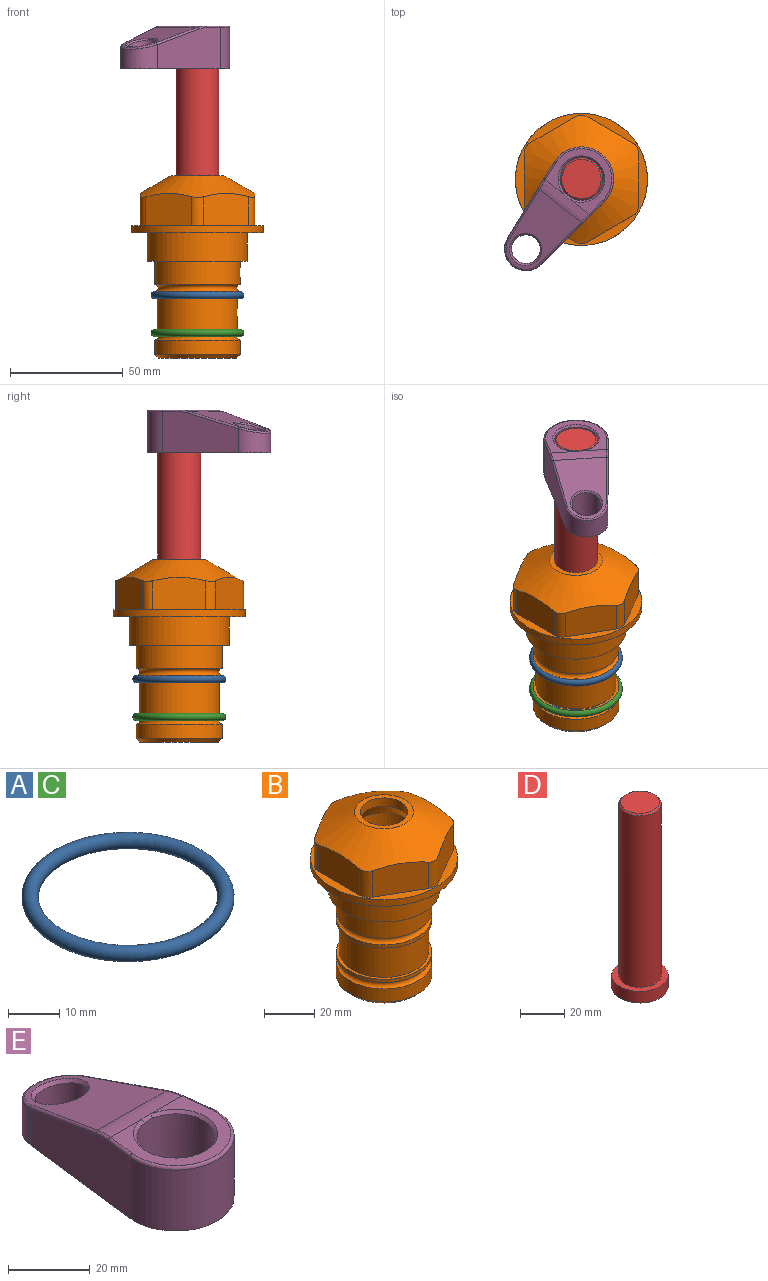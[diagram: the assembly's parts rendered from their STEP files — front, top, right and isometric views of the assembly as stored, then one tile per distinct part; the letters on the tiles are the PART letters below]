
ASSEMBLY  parts=5 mates=4
PART A: 1 faces, bbox 44.7x44.7x3.2 mm
  f0: torus R=19.05mm, axis (0,0,1), area 1193.9mm2
PART B: 36 faces, bbox 58.7x58.7x81 mm
  f0: cylinder r=17.78mm len=35.56mm, axis (0,0,1), area 1670.8mm2, adj f23,f24,f31
  f1: cylinder r=19.05mm len=38.1mm, axis (0,0,1), area 1191.9mm2, adj f26,f27,f30
  f2: plane 58.66x58.66mm, normal (0,0,-1), area 1150.6mm2, adj f3,f28
  f3: cylinder r=29.33mm len=58.66mm, axis (0,0,-1), area 585.1mm2, adj f2,f4
  f4: plane 58.66x58.66mm, normal (0,0,1), area 475.9mm2, adj f3,f5,f6,f7,f8,f9,f10,f11
  f5: plane 20.32x14.34mm, normal (-0.5,0.87,0), area 324.4mm2, adj f4,f15,f16,f17
  f6: plane 20.32x14.34mm, normal (0.5,0.87,0), area 324.4mm2, adj f4,f14,f15,f17
  f7: plane 23.48x14.34mm, normal (1,0,0), area 324.4mm2, adj f4,f13,f14,f17
  f8: plane 20.32x14.34mm, normal (0.5,-0.87,0), area 324.4mm2, adj f4,f12,f13,f17
  f9: plane 20.32x14.34mm, normal (-0.5,-0.87,0), area 324.4mm2, adj f4,f11,f12,f17
  f10: plane 23.48x14.34mm, normal (-1,0,0), area 324.4mm2, adj f4,f11,f16,f17
  f11: cylinder r=5.08mm len=12.85mm, axis (0,0,-1), area 67.2mm2, adj f4,f9,f10,f17
  f12: cylinder r=5.08mm len=12.85mm, axis (0,0,-1), area 67.2mm2, adj f4,f8,f9,f17
  f13: cylinder r=5.08mm len=12.85mm, axis (0,0,-1), area 67.2mm2, adj f4,f7,f8,f17
  f14: cylinder r=5.08mm len=12.85mm, axis (0,0,-1), area 67.2mm2, adj f4,f6,f7,f17
  f15: cylinder r=5.08mm len=12.85mm, axis (0,0,-1), area 67.2mm2, adj f4,f5,f6,f17
  f16: cylinder r=5.08mm len=12.85mm, axis (0,0,-1), area 67.2mm2, adj f4,f5,f10,f17
  f17: cone r=11.73mm half-angle=60deg, axis (0,0,-1), area 2071.8mm2, adj f5,f6,f7,f8,f9,f10,f11,f12
  f18: plane 23.46x23.46mm, normal (0,0,1), area 147.4mm2, adj f17,f35
  f19: plane 34.93x34.93mm, normal (0,0,-1), area 958mm2, adj f29
  f20: cylinder r=19.05mm len=38.1mm, axis (0,0,1), area 760.1mm2, adj f21,f29
  f21: torus R=19.05mm, axis (0,0,1), area 565.3mm2, adj f20,f22
  f22: cylinder r=19.05mm len=38.1mm, axis (0,0,1), area 190mm2, adj f21,f23
  f23: plane 38.1x38.1mm, normal (0,0,1), area 146.9mm2, adj f0,f22
  f24: plane 38.1x38.1mm, normal (0,0,-1), area 146.9mm2, adj f0,f25
  f25: cylinder r=19.05mm len=38.1mm, axis (0,0,1), area 190mm2, adj f24,f26
  f26: torus R=19.05mm, axis (0,0,1), area 565.3mm2, adj f1,f25
  f27: plane 44.45x44.45mm, normal (0,0,-1), area 411.7mm2, adj f1,f28
  f28: cylinder r=22.23mm len=44.45mm, axis (0,0,1), area 1773.5mm2, adj f2,f27
  f29: cone r=19.05mm half-angle=45deg, axis (0,0,1), area 257.5mm2, adj f19,f20
  f30: cylinder r=3.17mm len=6.75mm, axis (-1,0,0), area 128mm2, adj f1,f33
  f31: cylinder r=3.17mm len=6.35mm, axis (-1,0,0), area 102.5mm2, adj f0,f33
  f32: plane 25.4x25.4mm, normal (0,0,1), area 506.7mm2, adj f33
  f33: cylinder r=12.7mm len=66.42mm, axis (0,0,-1), area 5236.2mm2, adj f30,f31,f32,f34
  f34: cone r=9.53mm half-angle=30deg, axis (0,0,-1), area 443.4mm2, adj f33,f35
  f35: cylinder r=9.53mm len=19.05mm, axis (0,0,-1), area 240.9mm2, adj f18,f34
PART C: same geometry as A
PART D: 6 faces, bbox 25.4x25.4x101.6 mm
  f0: plane 17.46x17.46mm, normal (0,0,1), area 239.5mm2, adj f5
  f1: plane 25.4x25.4mm, normal (0,0,-1), area 506.7mm2, adj f2
  f2: cylinder r=12.7mm len=25.4mm, axis (0,0,1), area 506.7mm2, adj f1,f3
  f3: plane 25.4x25.4mm, normal (0,0,1), area 221.7mm2, adj f2,f4
  f4: cylinder r=9.53mm len=94.46mm, axis (0,0,1), area 5653mm2, adj f3,f5
  f5: cone r=8.73mm half-angle=45deg, axis (0,0,-1), area 64.4mm2, adj f0,f4
PART E: 31 faces, bbox 31.7x65.5x19.8 mm
  f0: plane 39.12x18.26mm, normal (0.99,0.12,0), area 612.2mm2, adj f1,f4,f7,f11,f13,f15
  f1: cylinder r=9.53mm len=18.91mm, axis (0,0,-1), area 296.1mm2, adj f0,f2,f7,f17
  f2: plane 39.12x18.26mm, normal (-0.99,0.12,0), area 612.2mm2, adj f1,f4,f7,f12,f14,f16
  f3: cylinder r=6.35mm len=12.7mm, axis (0,0,-1), area 362.4mm2, adj f7,f18
  f4: cylinder r=14.29mm len=28.58mm, axis (0,0,-1), area 882.2mm2, adj f0,f2,f7,f10
  f5: cylinder r=9.53mm len=19.05mm, axis (0,0,-1), area 1092.6mm2, adj f7,f19,f20
  f6: plane 26.99x23.69mm, normal (0,0,1), area 216.2mm2, adj f9,f10,f11,f12,f19
  f7: plane 63.5x28.58mm, normal (0,0,-1), area 661.8mm2, adj f0,f1,f2,f3,f4,f5,f22,f23
  f8: plane 33.52x23.6mm, normal (0,0.26,0.97), area 486mm2, adj f9,f15,f16,f17,f18
  f9: cylinder r=19.05mm len=24.72mm, axis (1,0,0), area 120.4mm2, adj f6,f8,f13,f14,f20
  f10: torus R=13.49mm, axis (0,0,1), area 59mm2, adj f4,f6,f11,f12
  f11: cylinder r=0.79mm len=8.67mm, axis (0.12,-0.99,0), area 10.8mm2, adj f0,f6,f10,f13
  f12: cylinder r=0.79mm len=8.67mm, axis (0.12,0.99,0), area 10.8mm2, adj f2,f6,f10,f14
  f13: bspline ~4.95x1.42mm, area 6.1mm2, adj f0,f9,f11,f15
  f14: bspline ~4.95x1.42mm, area 6.1mm2, adj f2,f9,f12,f16
  f15: cylinder r=0.79mm len=25.95mm, axis (0.12,-0.96,0.26), area 32.9mm2, adj f0,f8,f13,f17
  f16: cylinder r=0.79mm len=25.95mm, axis (0.12,0.96,-0.26), area 32.9mm2, adj f2,f8,f14,f17
  f17: bspline ~18.91x8.38mm, area 30mm2, adj f1,f8,f15,f16
  f18: bspline ~14.29x14.29mm, area 48.3mm2, adj f3,f8
  f19: cone r=9.53mm half-angle=45deg, axis (0,0,1), area 66.5mm2, adj f5,f6,f20
  f20: bspline ~3.22x0.96mm, area 3.5mm2, adj f5,f9,f19
  f21: plane 2.75x2.72mm, normal (0,0,-1), area 2.9mm2, adj f23,f25,f28
  f22: plane 23.05x15.88mm, normal (-0.99,-0.12,0), area 323.6mm2, adj f7,f25,f26,f27,f28,f29
  f23: plane 23.05x15.88mm, normal (0.99,-0.12,0), area 323.6mm2, adj f7,f21,f25,f27,f28,f30
  f24: cylinder r=9.53mm len=10.69mm, axis (0,0,-1), area 114.7mm2, adj f7,f27,f29,f30
  f25: cylinder r=12.7mm len=20.59mm, axis (0,0,-1), area 381.1mm2, adj f7,f21,f22,f23,f26,f28
  f26: plane 2.75x2.72mm, normal (0,0,-1), area 2.9mm2, adj f22,f25,f28
  f27: plane 19.72x18.37mm, normal (0,-0.26,-0.97), area 291.8mm2, adj f22,f23,f24,f28,f29,f30
  f28: cylinder r=15.88mm len=19.92mm, axis (1,0,0), area 54.8mm2, adj f21,f22,f23,f25,f26,f27
  f29: cylinder r=1.59mm len=11mm, axis (0,0,-1), area 34.7mm2, adj f7,f22,f24,f27
  f30: cylinder r=1.59mm len=11mm, axis (0,0,-1), area 34.7mm2, adj f7,f23,f24,f27
PLACE A t=(0,0,-3.18)mm
PLACE B at identity fixed
PLACE C t=(0,0,-20)mm
PLACE D rot(axis=(0,0,1),141.6deg) t=(0,0,27.55)mm
PLACE E rot(axis=(0,0,1),141.6deg) t=(0,0,28.35)mm
MATE fastened A.f0 <-> B.f0  axis (0,0,1) through (0,0,-27.69)mm
MATE cylindrical D.f2 <-> B.f0  axis (0,0,-1) through (0,0,-10.55)mm
MATE fastened C.f0 <-> B.f0  axis (0,0,1) through (0,0,-44.51)mm
MATE fastened D.f2 <-> E.f4  axis (0,0,1) through (0,0,91.05)mm
